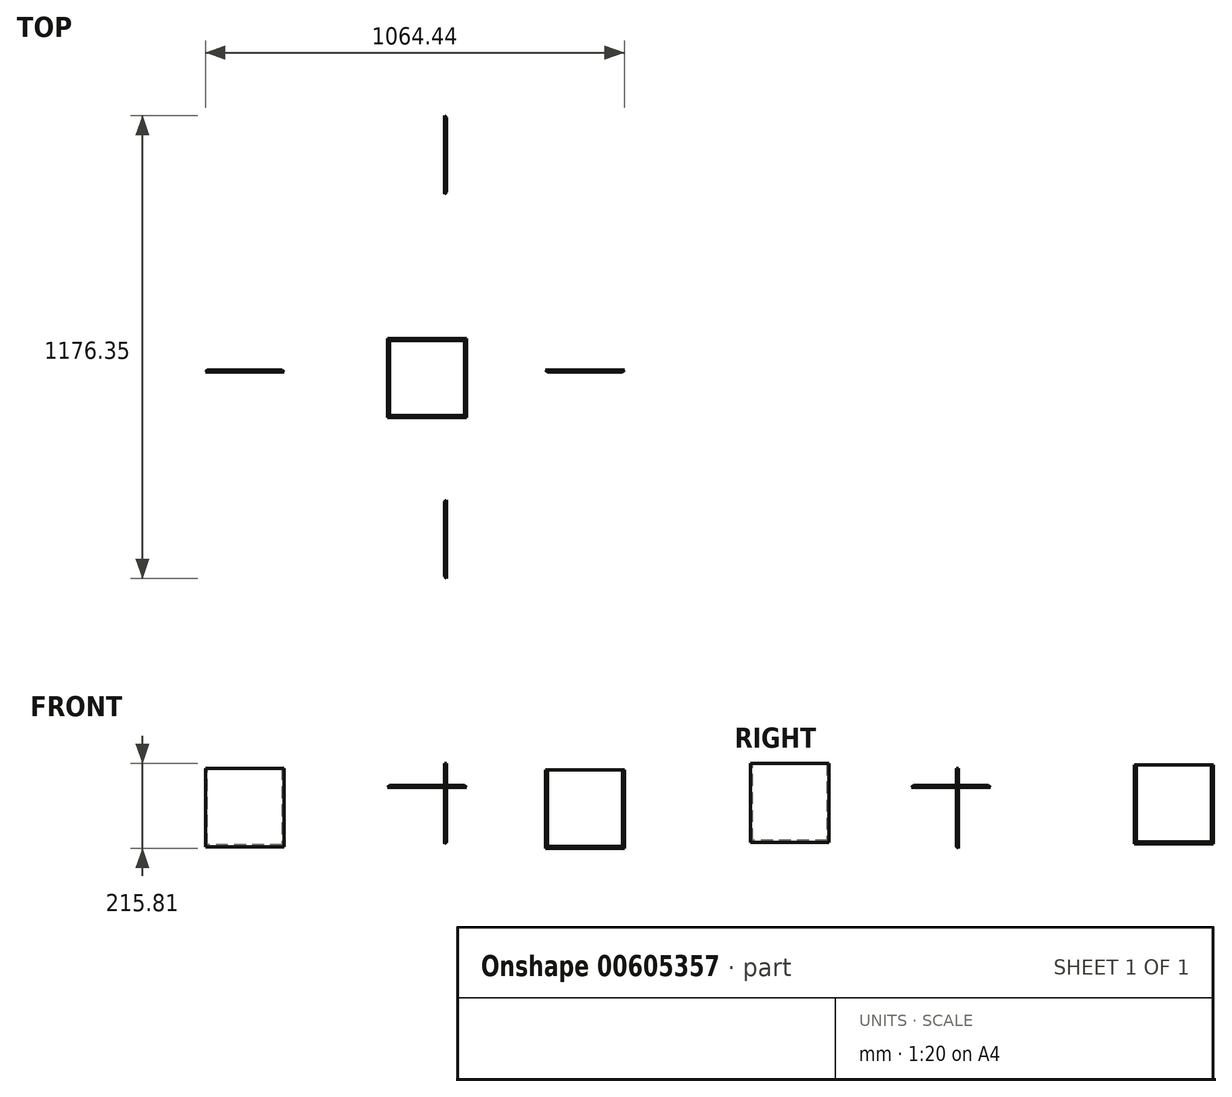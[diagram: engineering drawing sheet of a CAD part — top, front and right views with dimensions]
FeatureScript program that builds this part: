
annotation { "Feature Type Name" : "Feature", "Feature Type Description" : "" }
export const myFeature = defineFeature(function(context is Context, id is Id, definition is map)
    precondition{}
    {
        {
            var Q0;
            Q0=qCreatedBy(makeId("Top.planeOp"),FACE);
            var sketch = newSketch(context, id + "F0", { "sketchPlane" : qUnion([Q0])});
            skLineSegment(sketch, "E0.bottom", {"start": v(-145.11, 80.16) * mm, "end": v(54.89, 80.16) * mm});
            skLineSegment(sketch, "E0.top", {"start": v(-145.11, -119.84) * mm, "end": v(54.89, -119.84) * mm});
            skLineSegment(sketch, "E0.left", {"start": v(-145.11, 80.16) * mm, "end": v(-145.11, -119.84) * mm});
            skLineSegment(sketch, "E0.right", {"start": v(54.89, 80.16) * mm, "end": v(54.89, -119.84) * mm});
            skSolve(sketch);
        }
        {
            var Q0;
            Q0 = qSketchRegion(id + "F0", true);
            extrude(context, id + "F1", {"entities" : qUnion([Q0]), "depth" : 5 * mm, "offsetDistance" : 25 * mm});
        }
        {
            var Q0;
            Q0=makeQuery(id+"F1.opExtrude","CAP_EDGE",EDGE,{"disambiguationData":[OSD([sQuery(id+"F0.wireOp",EDGE,"E0.top")])],"isStart":false});
            var Q1;
            Q1=makeQuery(id+"F1.opExtrude","CAP_EDGE",EDGE,{"disambiguationData":[OSD([sQuery(id+"F0.wireOp",EDGE,"E0.right")])],"isStart":false});
            var Q2;
            Q2=makeQuery(id+"F1.opExtrude","CAP_EDGE",EDGE,{"disambiguationData":[OSD([sQuery(id+"F0.wireOp",EDGE,"E0.bottom")])],"isStart":false});
            var Q3;
            Q3=makeQuery(id+"F1.opExtrude","CAP_EDGE",EDGE,{"disambiguationData":[OSD([sQuery(id+"F0.wireOp",EDGE,"E0.left")])],"isStart":false});
            chamfer(context, id + "F2", {"entities" : qUnion([Q0, Q1, Q2, Q3]), "width" : 5 * mm, "tangentPropagation" : true});
        }
        {
            var Q0;
            Q0=qCreatedBy(makeId("Front.planeOp"),FACE);
            var sketch = newSketch(context, id + "F3", { "sketchPlane" : qUnion([Q0])});
            skLineSegment(sketch, "E1.bottom", {"start": v(256.29, 45.1) * mm, "end": v(456.29, 45.1) * mm});
            skLineSegment(sketch, "E1.top", {"start": v(256.29, -154.9) * mm, "end": v(456.29, -154.9) * mm});
            skLineSegment(sketch, "E1.left", {"start": v(256.29, 45.1) * mm, "end": v(256.29, -154.9) * mm});
            skLineSegment(sketch, "E1.right", {"start": v(456.29, 45.1) * mm, "end": v(456.29, -154.9) * mm});
            skSolve(sketch);
        }
        {
            var Q0;
            Q0 = qSketchRegion(id + "F3", true);
            extrude(context, id + "F4", {"entities" : qUnion([Q0]), "depth" : 5 * mm, "offsetDistance" : 25 * mm});
        }
        {
            var Q0;
            Q0=makeQuery(id+"F4.opExtrude","CAP_EDGE",EDGE,{"disambiguationData":[OSD([sQuery(id+"F3.wireOp",EDGE,"E1.top")])],"isStart":false});
            var Q1;
            Q1=makeQuery(id+"F4.opExtrude","CAP_EDGE",EDGE,{"disambiguationData":[OSD([sQuery(id+"F3.wireOp",EDGE,"E1.left")])],"isStart":false});
            var Q2;
            Q2=makeQuery(id+"F4.opExtrude","CAP_EDGE",EDGE,{"disambiguationData":[OSD([sQuery(id+"F3.wireOp",EDGE,"E1.right")])],"isStart":false});
            chamfer(context, id + "F5", {"entities" : qUnion([Q0, Q1, Q2]), "width" : 5 * mm, "tangentPropagation" : true});
        }
        {
            var Q0;
            Q0=qCreatedBy(makeId("Front.planeOp"),FACE);
            var sketch = newSketch(context, id + "F6", { "sketchPlane" : qUnion([Q0])});
            skLineSegment(sketch, "E2.bottom", {"start": v(-608.15, 48.65) * mm, "end": v(-408.15, 48.65) * mm});
            skLineSegment(sketch, "E2.top", {"start": v(-608.15, -151.35) * mm, "end": v(-408.15, -151.35) * mm});
            skLineSegment(sketch, "E2.left", {"start": v(-608.15, 48.65) * mm, "end": v(-608.15, -151.35) * mm});
            skLineSegment(sketch, "E2.right", {"start": v(-408.15, 48.65) * mm, "end": v(-408.15, -151.35) * mm});
            skSolve(sketch);
        }
        {
            var Q0;
            Q0 = qSketchRegion(id + "F6", true);
            extrude(context, id + "F7", {"entities" : qUnion([Q0]), "depth" : 5 * mm, "offsetDistance" : 25 * mm});
        }
        {
            var Q0;
            Q0=makeQuery(id+"F7.opExtrude","CAP_EDGE",EDGE,{"disambiguationData":[OSD([sQuery(id+"F6.wireOp",EDGE,"E2.right")])],"isStart":true});
            var Q1;
            Q1=makeQuery(id+"F7.opExtrude","CAP_EDGE",EDGE,{"disambiguationData":[OSD([sQuery(id+"F6.wireOp",EDGE,"E2.top")])],"isStart":true});
            var Q2;
            Q2=makeQuery(id+"F7.opExtrude","CAP_EDGE",EDGE,{"disambiguationData":[OSD([sQuery(id+"F6.wireOp",EDGE,"E2.left")])],"isStart":true});
            chamfer(context, id + "F8", {"entities" : qUnion([Q0, Q1, Q2]), "width" : 5 * mm, "tangentPropagation" : true});
        }
        {
            var Q0;
            Q0=qCreatedBy(makeId("Right.planeOp"),FACE);
            var sketch = newSketch(context, id + "F9", { "sketchPlane" : qUnion([Q0])});
            skLineSegment(sketch, "E3.bottom", {"start": v(447.06, 57.07) * mm, "end": v(647.06, 57.07) * mm});
            skLineSegment(sketch, "E3.top", {"start": v(447.06, -142.93) * mm, "end": v(647.06, -142.93) * mm});
            skLineSegment(sketch, "E3.left", {"start": v(447.06, 57.07) * mm, "end": v(447.06, -142.93) * mm});
            skLineSegment(sketch, "E3.right", {"start": v(647.06, 57.07) * mm, "end": v(647.06, -142.93) * mm});
            skLineSegment(sketch, "E4.bottom", {"start": v(-529.29, 60.91) * mm, "end": v(-329.29, 60.91) * mm});
            skLineSegment(sketch, "E4.top", {"start": v(-529.29, -139.09) * mm, "end": v(-329.29, -139.09) * mm});
            skLineSegment(sketch, "E4.left", {"start": v(-529.29, 60.91) * mm, "end": v(-529.29, -139.09) * mm});
            skLineSegment(sketch, "E4.right", {"start": v(-329.29, 60.91) * mm, "end": v(-329.29, -139.09) * mm});
            skSolve(sketch);
        }
        {
            var Q0;
            Q0 = qSketchRegion(id + "F9", true);
            extrude(context, id + "F10", {"entities" : qUnion([Q0]), "depth" : 5 * mm, "offsetDistance" : 25 * mm});
        }
        {
            var Q0;
            Q0=makeQuery(id+"F10.opExtrude","CAP_EDGE",EDGE,{"disambiguationData":[OSD([sQuery(id+"F9.wireOp",EDGE,"E3.left")])],"isStart":false});
            var Q1;
            Q1=makeQuery(id+"F10.opExtrude","CAP_EDGE",EDGE,{"disambiguationData":[OSD([sQuery(id+"F9.wireOp",EDGE,"E3.top")])],"isStart":false});
            var Q2;
            Q2=makeQuery(id+"F10.opExtrude","CAP_EDGE",EDGE,{"disambiguationData":[OSD([sQuery(id+"F9.wireOp",EDGE,"E3.right")])],"isStart":false});
            var Q3;
            Q3=makeQuery(id+"F10.opExtrude","CAP_EDGE",EDGE,{"disambiguationData":[OSD([sQuery(id+"F9.wireOp",EDGE,"E4.right")])],"isStart":true});
            var Q4;
            Q4=makeQuery(id+"F10.opExtrude","CAP_EDGE",EDGE,{"disambiguationData":[OSD([sQuery(id+"F9.wireOp",EDGE,"E4.top")])],"isStart":true});
            var Q5;
            Q5=makeQuery(id+"F10.opExtrude","CAP_EDGE",EDGE,{"disambiguationData":[OSD([sQuery(id+"F9.wireOp",EDGE,"E4.left")])],"isStart":true});
            chamfer(context, id + "F11", {"entities" : qUnion([Q0, Q1, Q2, Q3, Q4, Q5]), "width" : 5 * mm, "tangentPropagation" : true});
        }
    });
